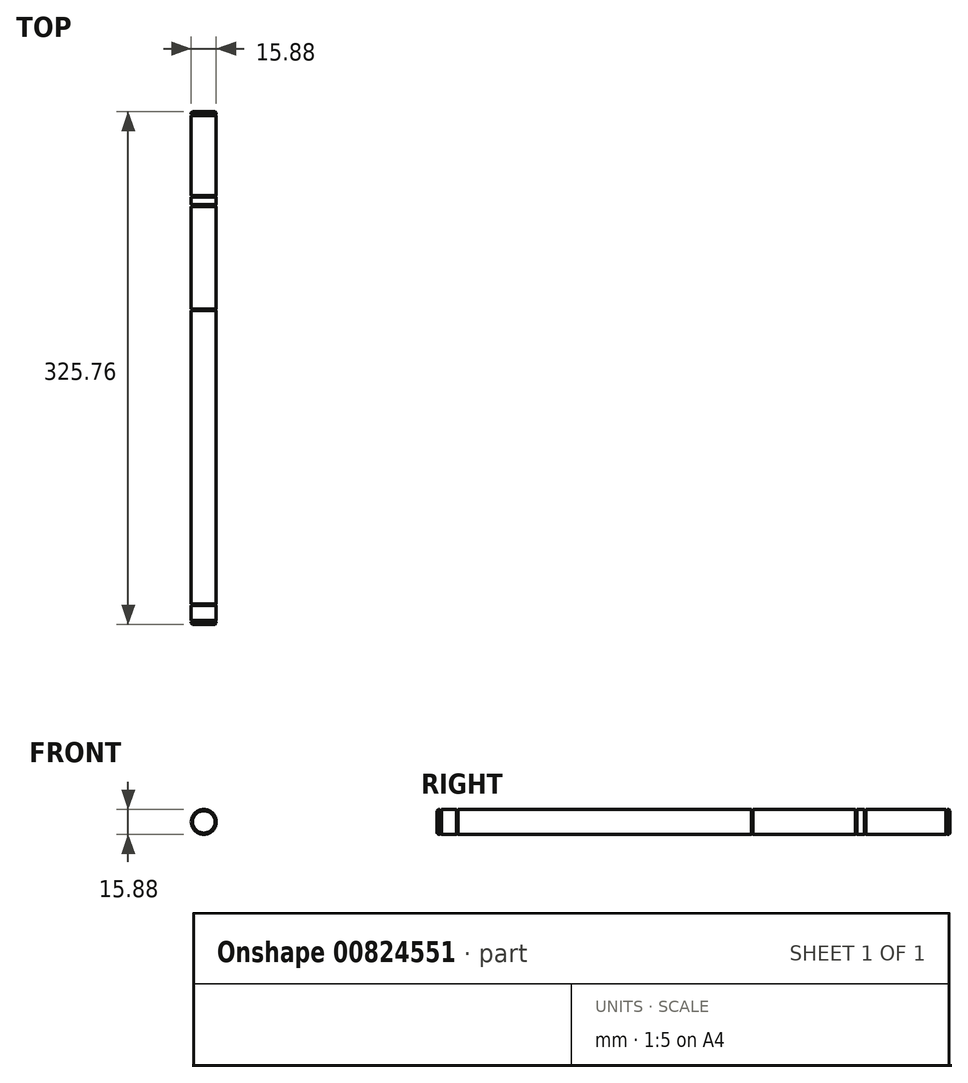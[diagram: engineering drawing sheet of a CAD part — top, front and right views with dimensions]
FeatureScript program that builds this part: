
annotation { "Feature Type Name" : "Feature", "Feature Type Description" : "" }
export const myFeature = defineFeature(function(context is Context, id is Id, definition is map)
    precondition{}
    {
        {
            var Q0;
            Q0=qCreatedBy(makeId("Front.planeOp"),FACE);
            var sketch = newSketch(context, id + "F0", { "sketchPlane" : qUnion([Q0])});
            skCircle(sketch, "E0", {"center": v(0, 0) * mm, "radius": 7.94 * mm});
            skSolve(sketch);
        }
        {
            var Q0;
            Q0=makeQuery(id+"F0.imprint","IMPRINT",FACE,{"disambiguationData":[TD([[makeQuery(id+"F0.imprint","IMPRINT",EDGE,{"derivedFrom":sQuery(id+"F0.wireOp",EDGE,"E0")}),1.0]])]});
            extrude(context, id + "F1", {"entities" : qUnion([Q0]), "depth" : 1.59 * mm, "offsetDistance" : 25.4 * mm});
        }
        {
            var Q0;
            Q0=makeQuery(id+"F1.opExtrude","CAP_FACE",FACE,{"disambiguationData":[OSD([sQuery(id+"F0.wireOp",EDGE,"E0")])],"isStart":false});
            var sketch = newSketch(context, id + "F2", { "sketchPlane" : qUnion([Q0])});
            skCircle(sketch, "E1", {"center": v(0, 0) * mm, "radius": 7.47 * mm});
            skSolve(sketch);
        }
        {
            var Q0;
            Q0=makeQuery(id+"F2.imprint","IMPRINT",FACE,{"disambiguationData":[TD([[makeQuery(id+"F2.imprint","IMPRINT",EDGE,{"derivedFrom":sQuery(id+"F2.wireOp",EDGE,"E1")}),1.0]])]});
            extrude(context, id + "F3", {"entities" : qUnion([Q0]), "operationType" : NewBodyOperationType.ADD, "depth" : 1.02 * mm, "offsetDistance" : 25.4 * mm});
        }
        {
            var Q0;
            Q0=makeQuery(id+"F3.opExtrude","CAP_FACE",FACE,{"disambiguationData":[OSD([sQuery(id+"F2.wireOp",EDGE,"E1")])],"isStart":false});
            var sketch = newSketch(context, id + "F4", { "sketchPlane" : qUnion([Q0])});
            skCircle(sketch, "E2", {"center": v(0, 0) * mm, "radius": 7.94 * mm});
            skSolve(sketch);
        }
        {
            var Q0;
            Q0=qSketchRegion(id+"F4",true);
            extrude(context, id + "F5", {"entities" : qUnion([Q0]), "operationType" : NewBodyOperationType.ADD, "depth" : 50.8 * mm, "offsetDistance" : 25.4 * mm});
        }
        {
            var Q0;
            Q0=makeQuery(id+"F5.opExtrude","CAP_FACE",FACE,{"disambiguationData":[OSD([sQuery(id+"F4.wireOp",EDGE,"E2")])],"isStart":false});
            var sketch = newSketch(context, id + "F6", { "sketchPlane" : qUnion([Q0])});
            skCircle(sketch, "E3", {"center": v(0, 0) * mm, "radius": 7.47 * mm});
            skSolve(sketch);
        }
        {
            var Q0;
            Q0=makeQuery(id+"F6.imprint","IMPRINT",FACE,{"disambiguationData":[TD([[makeQuery(id+"F6.imprint","IMPRINT",EDGE,{"derivedFrom":sQuery(id+"F6.wireOp",EDGE,"E3")}),1.0]])]});
            extrude(context, id + "F7", {"entities" : qUnion([Q0]), "operationType" : NewBodyOperationType.ADD, "depth" : 1.02 * mm, "offsetDistance" : 25.4 * mm});
        }
        {
            var Q0;
            Q0=makeQuery(id+"F7.opExtrude","CAP_FACE",FACE,{"disambiguationData":[OSD([sQuery(id+"F6.wireOp",EDGE,"E3")])],"isStart":false});
            var sketch = newSketch(context, id + "F8", { "sketchPlane" : qUnion([Q0])});
            skCircle(sketch, "E4", {"center": v(0, 0) * mm, "radius": 7.94 * mm});
            skSolve(sketch);
        }
        {
            var Q0;
            Q0=qSketchRegion(id+"F8",true);
            extrude(context, id + "F9", {"entities" : qUnion([Q0]), "operationType" : NewBodyOperationType.ADD, "depth" : 4.76 * mm, "offsetDistance" : 25.4 * mm});
        }
        {
            var Q0;
            Q0=makeQuery(id+"F9.opExtrude","CAP_FACE",FACE,{"disambiguationData":[OSD([sQuery(id+"F8.wireOp",EDGE,"E4")])],"isStart":false});
            var sketch = newSketch(context, id + "F10", { "sketchPlane" : qUnion([Q0])});
            skCircle(sketch, "E5", {"center": v(0, 0) * mm, "radius": 7.47 * mm});
            skSolve(sketch);
        }
        {
            var Q0;
            Q0=makeQuery(id+"F10.imprint","IMPRINT",FACE,{"disambiguationData":[TD([[makeQuery(id+"F10.imprint","IMPRINT",EDGE,{"derivedFrom":sQuery(id+"F10.wireOp",EDGE,"E5")}),1.0]])]});
            extrude(context, id + "F11", {"entities" : qUnion([Q0]), "operationType" : NewBodyOperationType.ADD, "depth" : 1.02 * mm, "offsetDistance" : 25.4 * mm});
        }
        {
            var Q0;
            Q0=makeQuery(id+"F11.opExtrude","CAP_FACE",FACE,{"disambiguationData":[OSD([sQuery(id+"F10.wireOp",EDGE,"E5")])],"isStart":false});
            var sketch = newSketch(context, id + "F12", { "sketchPlane" : qUnion([Q0])});
            skCircle(sketch, "E6", {"center": v(0, 0) * mm, "radius": 7.94 * mm});
            skSolve(sketch);
        }
        {
            var Q0;
            Q0=qSketchRegion(id+"F12",true);
            extrude(context, id + "F13", {"entities" : qUnion([Q0]), "operationType" : NewBodyOperationType.ADD, "depth" : 65.1 * mm, "offsetDistance" : 25.4 * mm});
        }
        {
            var Q0;
            Q0=makeQuery(id+"F13.opExtrude","CAP_FACE",FACE,{"disambiguationData":[OSD([sQuery(id+"F12.wireOp",EDGE,"E6")])],"isStart":false});
            var sketch = newSketch(context, id + "F14", { "sketchPlane" : qUnion([Q0])});
            skCircle(sketch, "E7", {"center": v(0, 0) * mm, "radius": 7.47 * mm});
            skSolve(sketch);
        }
        {
            var Q0;
            Q0=makeQuery(id+"F14.imprint","IMPRINT",FACE,{"disambiguationData":[TD([[makeQuery(id+"F14.imprint","IMPRINT",EDGE,{"derivedFrom":sQuery(id+"F14.wireOp",EDGE,"E7")}),1.0]])]});
            extrude(context, id + "F15", {"entities" : qUnion([Q0]), "operationType" : NewBodyOperationType.ADD, "depth" : 1.02 * mm, "offsetDistance" : 25.4 * mm});
        }
        {
            var Q0;
            Q0=makeQuery(id+"F15.opExtrude","CAP_FACE",FACE,{"disambiguationData":[OSD([sQuery(id+"F14.wireOp",EDGE,"E7")])],"isStart":false});
            var sketch = newSketch(context, id + "F16", { "sketchPlane" : qUnion([Q0])});
            skCircle(sketch, "E8", {"center": v(0, 0) * mm, "radius": 7.94 * mm});
            skSolve(sketch);
        }
        {
            var Q0;
            Q0=qSketchRegion(id+"F16",true);
            extrude(context, id + "F17", {"entities" : qUnion([Q0]), "operationType" : NewBodyOperationType.ADD, "depth" : 186.3 * mm, "offsetDistance" : 25.4 * mm});
        }
        {
            var Q0;
            Q0=makeQuery(id+"F17.opExtrude","CAP_FACE",FACE,{"disambiguationData":[OSD([sQuery(id+"F16.wireOp",EDGE,"E8")])],"isStart":false});
            var sketch = newSketch(context, id + "F18", { "sketchPlane" : qUnion([Q0])});
            skCircle(sketch, "E9", {"center": v(0, 0) * mm, "radius": 7.47 * mm});
            skSolve(sketch);
        }
        {
            var Q0;
            Q0=makeQuery(id+"F18.imprint","IMPRINT",FACE,{"disambiguationData":[TD([[makeQuery(id+"F18.imprint","IMPRINT",EDGE,{"derivedFrom":sQuery(id+"F18.wireOp",EDGE,"E9")}),1.0]])]});
            extrude(context, id + "F19", {"entities" : qUnion([Q0]), "operationType" : NewBodyOperationType.ADD, "depth" : 1.02 * mm, "offsetDistance" : 25.4 * mm});
        }
        {
            var Q0;
            Q0=makeQuery(id+"F19.opExtrude","CAP_FACE",FACE,{"disambiguationData":[OSD([sQuery(id+"F18.wireOp",EDGE,"E9")])],"isStart":false});
            var sketch = newSketch(context, id + "F20", { "sketchPlane" : qUnion([Q0])});
            skCircle(sketch, "E10", {"center": v(0, 0) * mm, "radius": 7.94 * mm});
            skSolve(sketch);
        }
        {
            var Q0;
            Q0=qSketchRegion(id+"F20",true);
            extrude(context, id + "F21", {"entities" : qUnion([Q0]), "operationType" : NewBodyOperationType.ADD, "depth" : 9.52 * mm, "offsetDistance" : 25.4 * mm});
        }
        {
            var Q0;
            Q0=makeQuery(id+"F21.opExtrude","CAP_FACE",FACE,{"disambiguationData":[OSD([sQuery(id+"F20.wireOp",EDGE,"E10")])],"isStart":false});
            var sketch = newSketch(context, id + "F22", { "sketchPlane" : qUnion([Q0])});
            skCircle(sketch, "E11", {"center": v(0, 0) * mm, "radius": 7.47 * mm});
            skSolve(sketch);
        }
        {
            var Q0;
            Q0=makeQuery(id+"F22.imprint","IMPRINT",FACE,{"disambiguationData":[TD([[makeQuery(id+"F22.imprint","IMPRINT",EDGE,{"derivedFrom":sQuery(id+"F22.wireOp",EDGE,"E11")}),1.0]])]});
            extrude(context, id + "F23", {"entities" : qUnion([Q0]), "operationType" : NewBodyOperationType.ADD, "depth" : 1.02 * mm, "offsetDistance" : 25.4 * mm});
        }
        {
            var Q0;
            Q0=makeQuery(id+"F23.opExtrude","CAP_FACE",FACE,{"disambiguationData":[OSD([sQuery(id+"F22.wireOp",EDGE,"E11")])],"isStart":false});
            var sketch = newSketch(context, id + "F24", { "sketchPlane" : qUnion([Q0])});
            skCircle(sketch, "E12", {"center": v(0, 0) * mm, "radius": 7.94 * mm});
            skSolve(sketch);
        }
        {
            var Q0;
            Q0=qSketchRegion(id+"F24",true);
            extrude(context, id + "F25", {"entities" : qUnion([Q0]), "operationType" : NewBodyOperationType.ADD, "depth" : 1.59 * mm, "offsetDistance" : 25.4 * mm});
        }
        {
            var Q0;
            Q0=makeQuery(id+"F25.opExtrude","CAP_EDGE",EDGE,{"disambiguationData":[OSD([sQuery(id+"F24.wireOp",EDGE,"E12")])],"isStart":false});
            var Q1;
            Q1=makeQuery(id+"F1.opExtrude","CAP_EDGE",EDGE,{"disambiguationData":[OSD([sQuery(id+"F0.wireOp",EDGE,"E0")])],"isStart":true});
            chamfer(context, id + "F26", {"entities" : qUnion([Q0, Q1]), "width" : 0.8 * mm, "tangentPropagation" : true});
        }
    });
